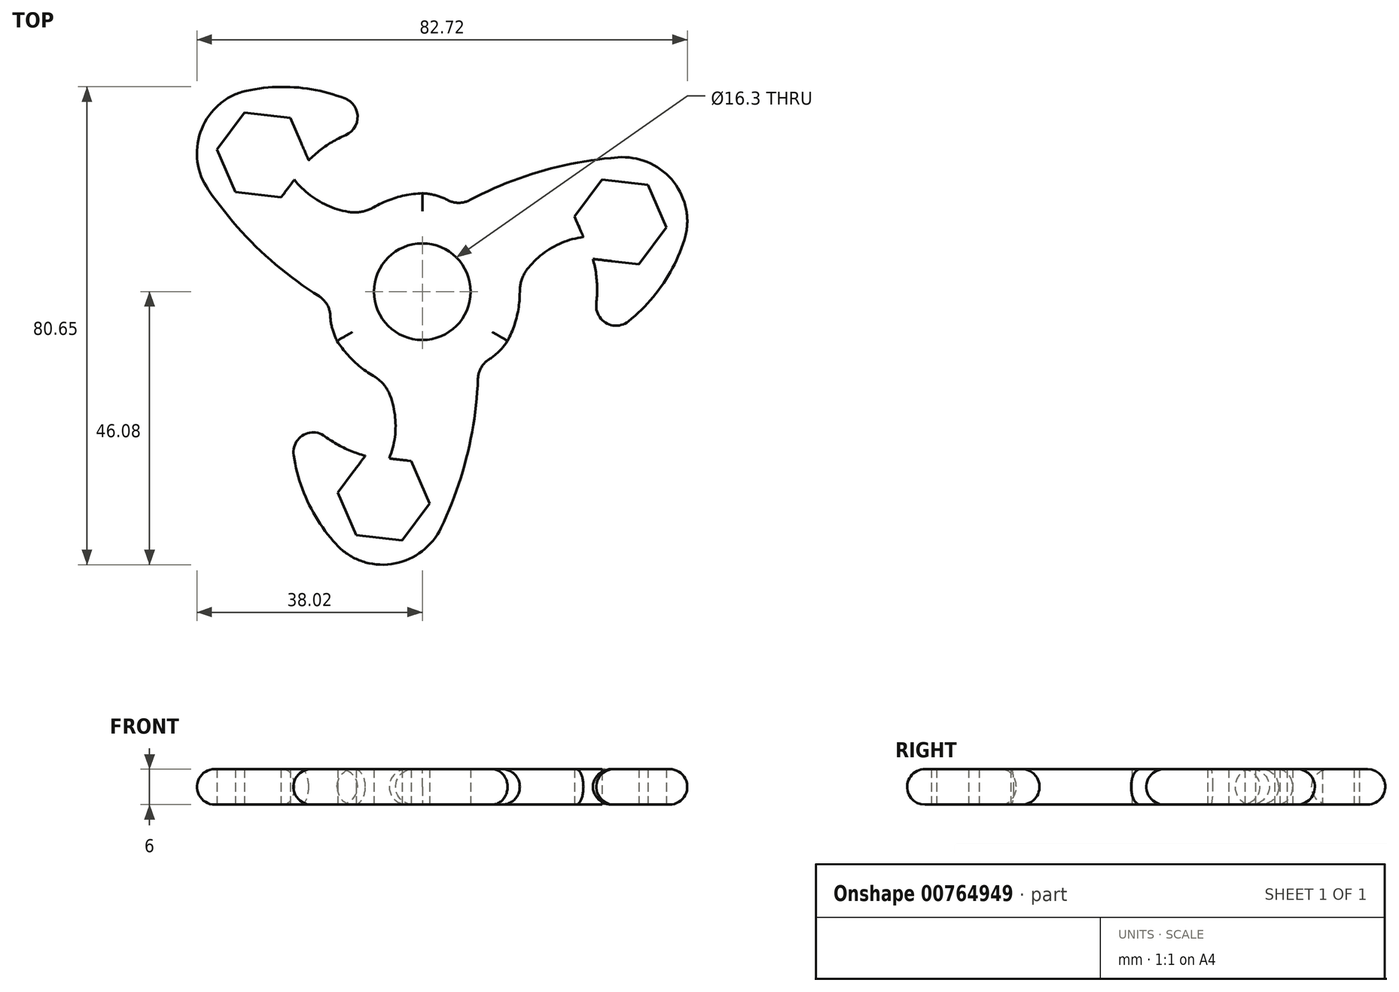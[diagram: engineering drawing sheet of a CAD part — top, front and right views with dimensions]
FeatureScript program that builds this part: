
annotation { "Feature Type Name" : "Feature", "Feature Type Description" : "" }
export const myFeature = defineFeature(function(context is Context, id is Id, definition is map)
    precondition{}
    {
        {
            var Q0;
            Q0=qCreatedBy(makeId("Top.planeOp"),FACE);
            var sketch = newSketch(context, id + "F0", { "sketchPlane" : qUnion([Q0])});
            skCircle(sketch, "E0", {"center": v(0, 0) * mm, "radius": 8.15 * mm});
            skLineSegment(sketch, "E1", {"start": v(0, 0) * mm, "end": v(0, -74.99) * mm});
            skLineSegment(sketch, "E2", {"start": v(0, -74.99) * mm, "end": v(0, 0) * mm});
            skLineSegment(sketch, "E3", {"start": v(0, 42.8) * mm, "end": v(0, 0) * mm, "construction": true});
            skLineSegment(sketch, "E4", {"start": v(0, 0) * mm, "end": v(33.8, -19.51) * mm, "construction": true});
            skPoint(sketch, "E5", {"position": v(0, 8.15) * mm});
            skPoint(sketch, "E6", {"position": v(7.06, -4.07) * mm});
            skArc(sketch, "E7.cCircle", {"start": v(38.84, 7.74) * mm, "mid": v(39, 7.97) * mm, "end": v(39.15, 8.2) * mm});
            skLineSegment(sketch, "E7.0", {"start": v(41.17, 10.87) * mm, "end": v(36.52, 4.62) * mm});
            skLineSegment(sketch, "E7.1", {"start": v(36.52, 4.62) * mm, "end": v(28.78, 5.52) * mm});
            skLineSegment(sketch, "E7.2", {"start": v(27.17, 9.24) * mm, "end": v(25.69, 12.68) * mm});
            skLineSegment(sketch, "E7.3", {"start": v(25.69, 12.68) * mm, "end": v(30.34, 18.93) * mm});
            skLineSegment(sketch, "E7.4", {"start": v(30.34, 18.93) * mm, "end": v(38.08, 18.03) * mm});
            skLineSegment(sketch, "E7.5", {"start": v(38.08, 18.03) * mm, "end": v(41.17, 10.87) * mm});
            skPoint(sketch, "E7.0.midPoint", {"position": v(38.84, 7.74) * mm});
            skPoint(sketch, "E8", {"position": v(32.96, 22.67) * mm});
            skCircle(sketch, "E9", {"center": v(0, 0) * mm, "radius": 40 * mm, "construction": true});
            skArc(sketch, "E10", {"start": v(4.28, 15.46) * mm, "mid": v(2.2, 16.27) * mm, "end": v(0, 16.6) * mm});
            skArc(sketch, "E11", {"start": v(4.28, 15.46) * mm, "mid": v(6.14, 15) * mm, "end": v(8, 15.46) * mm});
            skArc(sketch, "E12", {"start": v(32.96, 22.67) * mm, "mid": v(20.11, 20.34) * mm, "end": v(8, 15.46) * mm});
            skArc(sketch, "E13", {"start": v(44.2, 15.1) * mm, "mid": v(39.9, 20.84) * mm, "end": v(32.96, 22.67) * mm});
            skArc(sketch, "E14", {"start": v(44.2, 8.73) * mm, "mid": v(44.7, 11.92) * mm, "end": v(44.2, 15.1) * mm});
            skArc(sketch, "E15", {"start": v(34.76, -5) * mm, "mid": v(40.5, 1.17) * mm, "end": v(44.2, 8.73) * mm});
            skArc(sketch, "E16", {"start": v(29.35, -2) * mm, "mid": v(31.05, -5.31) * mm, "end": v(34.76, -5) * mm});
            skPoint(sketch, "E17.endSnap0", {"position": v(28.26, 3.15) * mm});
            skArc(sketch, "E18", {"start": v(29.35, -2) * mm, "mid": v(29.44, 1.8) * mm, "end": v(28.78, 5.52) * mm});
            skArc(sketch, "E19", {"start": v(17.92, 4.08) * mm, "mid": v(16.82, 2.17) * mm, "end": v(16.44, 0) * mm});
            skArc(sketch, "E20", {"start": v(14.38, -8.3) * mm, "mid": v(15.92, -4.28) * mm, "end": v(16.44, 0) * mm});
            skArc(sketch, "E21", {"start": v(27.17, 9.24) * mm, "mid": v(22.06, 7.52) * mm, "end": v(17.92, 4.08) * mm});
            skArc(sketch, "E22.1.0", {"start": v(-15.53, -4.03) * mm, "mid": v(-15.2, -6.23) * mm, "end": v(-14.38, -8.3) * mm});
            skArc(sketch, "E22.1.1", {"start": v(-15.53, -4.03) * mm, "mid": v(-16.06, -2.18) * mm, "end": v(-17.4, -0.8) * mm});
            skArc(sketch, "E22.1.2", {"start": v(-36.1, 17.21) * mm, "mid": v(-27.67, 7.25) * mm, "end": v(-17.4, -0.8) * mm});
            skArc(sketch, "E22.1.3", {"start": v(-35.18, 30.72) * mm, "mid": v(-38, 24.13) * mm, "end": v(-36.1, 17.21) * mm});
            skArc(sketch, "E22.1.4", {"start": v(-29.66, 33.91) * mm, "mid": v(-32.67, 32.75) * mm, "end": v(-35.18, 30.72) * mm});
            skArc(sketch, "E22.1.5", {"start": v(-13.05, 32.6) * mm, "mid": v(-21.26, 34.48) * mm, "end": v(-29.66, 33.91) * mm});
            skArc(sketch, "E22.1.6", {"start": v(-12.95, 26.42) * mm, "mid": v(-10.92, 29.55) * mm, "end": v(-13.05, 32.6) * mm});
            skArc(sketch, "E22.1.7", {"start": v(-12.95, 26.42) * mm, "mid": v(-16.27, 24.6) * mm, "end": v(-19.17, 22.16) * mm});
            skLineSegment(sketch, "E22.1.8", {"start": v(-22.26, 29.32) * mm, "end": v(-19.17, 22.16) * mm});
            skLineSegment(sketch, "E22.1.9", {"start": v(-30, 30.22) * mm, "end": v(-22.26, 29.32) * mm});
            skLineSegment(sketch, "E22.1.10", {"start": v(-34.65, 23.97) * mm, "end": v(-30, 30.22) * mm});
            skLineSegment(sketch, "E22.1.11", {"start": v(-31.56, 16.81) * mm, "end": v(-34.65, 23.97) * mm});
            skLineSegment(sketch, "E22.1.12", {"start": v(-23.82, 15.9) * mm, "end": v(-31.56, 16.81) * mm});
            skLineSegment(sketch, "E22.1.13", {"start": v(-21.59, 18.91) * mm, "end": v(-23.82, 15.9) * mm});
            skArc(sketch, "E22.1.14", {"start": v(-21.59, 18.91) * mm, "mid": v(-17.55, 15.34) * mm, "end": v(-12.5, 13.48) * mm});
            skArc(sketch, "E22.1.15", {"start": v(-12.5, 13.48) * mm, "mid": v(-10.29, 13.48) * mm, "end": v(-8.22, 14.24) * mm});
            skArc(sketch, "E22.1.16", {"start": v(0, 16.6) * mm, "mid": v(-4.26, 15.93) * mm, "end": v(-8.22, 14.24) * mm});
            skArc(sketch, "E22.2.0", {"start": v(11.25, -11.43) * mm, "mid": v(13, -10.04) * mm, "end": v(14.38, -8.3) * mm});
            skArc(sketch, "E22.2.1", {"start": v(11.25, -11.43) * mm, "mid": v(9.92, -12.82) * mm, "end": v(9.39, -14.67) * mm});
            skArc(sketch, "E22.2.2", {"start": v(3.15, -39.88) * mm, "mid": v(7.56, -27.6) * mm, "end": v(9.39, -14.67) * mm});
            skArc(sketch, "E22.2.3", {"start": v(-9.02, -45.83) * mm, "mid": v(-1.9, -44.97) * mm, "end": v(3.15, -39.88) * mm});
            skArc(sketch, "E22.2.4", {"start": v(-14.54, -42.64) * mm, "mid": v(-12.03, -44.67) * mm, "end": v(-9.02, -45.83) * mm});
            skArc(sketch, "E22.2.5", {"start": v(-21.7, -27.6) * mm, "mid": v(-19.23, -35.65) * mm, "end": v(-14.54, -42.64) * mm});
            skArc(sketch, "E22.2.6", {"start": v(-16.4, -24.42) * mm, "mid": v(-20.13, -24.23) * mm, "end": v(-21.7, -27.6) * mm});
            skArc(sketch, "E22.2.7", {"start": v(-16.4, -24.42) * mm, "mid": v(-13.17, -26.39) * mm, "end": v(-9.6, -27.68) * mm});
            skLineSegment(sketch, "E22.2.8", {"start": v(-14.26, -33.93) * mm, "end": v(-9.6, -27.68) * mm});
            skLineSegment(sketch, "E22.2.9", {"start": v(-11.17, -41.1) * mm, "end": v(-14.26, -33.93) * mm});
            skLineSegment(sketch, "E22.2.10", {"start": v(-3.43, -42) * mm, "end": v(-11.17, -41.1) * mm});
            skLineSegment(sketch, "E22.2.11", {"start": v(1.22, -35.74) * mm, "end": v(-3.43, -42) * mm});
            skLineSegment(sketch, "E22.2.12", {"start": v(-1.86, -28.58) * mm, "end": v(1.22, -35.74) * mm});
            skLineSegment(sketch, "E22.2.13", {"start": v(-5.58, -28.15) * mm, "end": v(-1.86, -28.58) * mm});
            skArc(sketch, "E22.2.14", {"start": v(-5.58, -28.15) * mm, "mid": v(-4.51, -22.87) * mm, "end": v(-5.42, -17.56) * mm});
            skArc(sketch, "E22.2.15", {"start": v(-5.42, -17.56) * mm, "mid": v(-6.53, -15.65) * mm, "end": v(-8.22, -14.24) * mm});
            skArc(sketch, "E22.2.16", {"start": v(-14.38, -8.3) * mm, "mid": v(-11.66, -11.65) * mm, "end": v(-8.22, -14.24) * mm});
            skLineSegment(sketch, "E23", {"start": v(0, 16.6) * mm, "end": v(7.86, 16.33) * mm, "construction": true});
            skLineSegment(sketch, "E24", {"start": v(14.38, -8.3) * mm, "end": v(16.97, -3.42) * mm, "construction": true});
            skSolve(sketch);
        }
        {
            var Q0;
            Q0=makeQuery(id+"F0.imprint","IMPRINT",FACE,{"disambiguationData":[TD([[makeQuery(id+"F0.imprint","IMPRINT",EDGE,{"derivedFrom":sQuery(id+"F0.wireOp",EDGE,"E0")}),-1.0]])]});
            var Q1;
            {var subQ0=sQuery(id+"F0.wireOp",EDGE,"E22.2.4");Q1=makeQuery(id+"F0.imprint","IMPRINT",FACE,{"disambiguationData":[TD([[makeQuery(id+"F0.imprint","IMPRINT",EDGE,{"derivedFrom":subQ0}),1.0]])]});}
            extrude(context, id + "F1", {"entities" : qUnion([Q0, Q1]), "depth" : 6 * mm, "offsetDistance" : 25 * mm});
        }
        {
            var Q0;
            Q0=makeQuery(id+"F1.opExtrude","CAP_EDGE",EDGE,{"disambiguationData":[OSD([sQuery(id+"F0.wireOp",EDGE,"E22.1.5")])],"isStart":false});
            var Q1;
            Q1=makeQuery(id+"F1.opExtrude","CAP_EDGE",EDGE,{"disambiguationData":[OSD([sQuery(id+"F0.wireOp",EDGE,"E22.1.14")])],"isStart":false});
            var Q2;
            Q2=makeQuery(id+"F1.opExtrude","CAP_EDGE",EDGE,{"disambiguationData":[OSD([sQuery(id+"F0.wireOp",EDGE,"E10")])],"isStart":false});
            var Q3;
            Q3=makeQuery(id+"F1.opExtrude","CAP_EDGE",EDGE,{"disambiguationData":[OSD([sQuery(id+"F0.wireOp",EDGE,"E12")])],"isStart":false});
            var Q4;
            Q4=makeQuery(id+"F1.opExtrude","CAP_EDGE",EDGE,{"disambiguationData":[OSD([sQuery(id+"F0.wireOp",EDGE,"E21")])],"isStart":false});
            var Q5;
            Q5=makeQuery(id+"F1.opExtrude","CAP_EDGE",EDGE,{"disambiguationData":[OSD([sQuery(id+"F0.wireOp",EDGE,"E19")])],"isStart":false});
            var Q6;
            Q6=makeQuery(id+"F1.opExtrude","CAP_EDGE",EDGE,{"disambiguationData":[OSD([sQuery(id+"F0.wireOp",EDGE,"E22.2.0")])],"isStart":false});
            var Q7;
            Q7=makeQuery(id+"F1.opExtrude","CAP_EDGE",EDGE,{"disambiguationData":[OSD([sQuery(id+"F0.wireOp",EDGE,"E22.2.16")])],"isStart":false});
            fillet(context, id + "F2", {"entities" : qUnion([Q0, Q1, Q2, Q3, Q4, Q5, Q6, Q7]), "radius" : 3 * mm, "tangentPropagation" : true, "allowEdgeOverflow" : false});
        }
        {
            var Q0;
            Q0=makeQuery(id+"F1.opExtrude","CAP_EDGE",EDGE,{"disambiguationData":[OSD([sQuery(id+"F0.wireOp",EDGE,"E22.2.2")])],"isStart":true});
            var Q1;
            Q1=makeQuery(id+"F1.opExtrude","CAP_EDGE",EDGE,{"disambiguationData":[OSD([sQuery(id+"F0.wireOp",EDGE,"E12")])],"isStart":true});
            var Q2;
            Q2=makeQuery(id+"F1.opExtrude","CAP_EDGE",EDGE,{"disambiguationData":[OSD([sQuery(id+"F0.wireOp",EDGE,"E20")])],"isStart":true});
            var Q3;
            Q3=makeQuery(id+"F1.opExtrude","CAP_EDGE",EDGE,{"disambiguationData":[OSD([sQuery(id+"F0.wireOp",EDGE,"E22.1.14")])],"isStart":true});
            var Q4;
            Q4=makeQuery(id+"F1.opExtrude","CAP_EDGE",EDGE,{"disambiguationData":[OSD([sQuery(id+"F0.wireOp",EDGE,"E22.1.5")])],"isStart":true});
            var Q5;
            Q5=makeQuery(id+"F1.opExtrude","CAP_EDGE",EDGE,{"disambiguationData":[OSD([sQuery(id+"F0.wireOp",EDGE,"E22.2.15")])],"isStart":true});
            fillet(context, id + "F3", {"entities" : qUnion([Q0, Q1, Q2, Q3, Q4, Q5]), "radius" : 3 * mm, "tangentPropagation" : true, "allowEdgeOverflow" : false});
        }
    });
